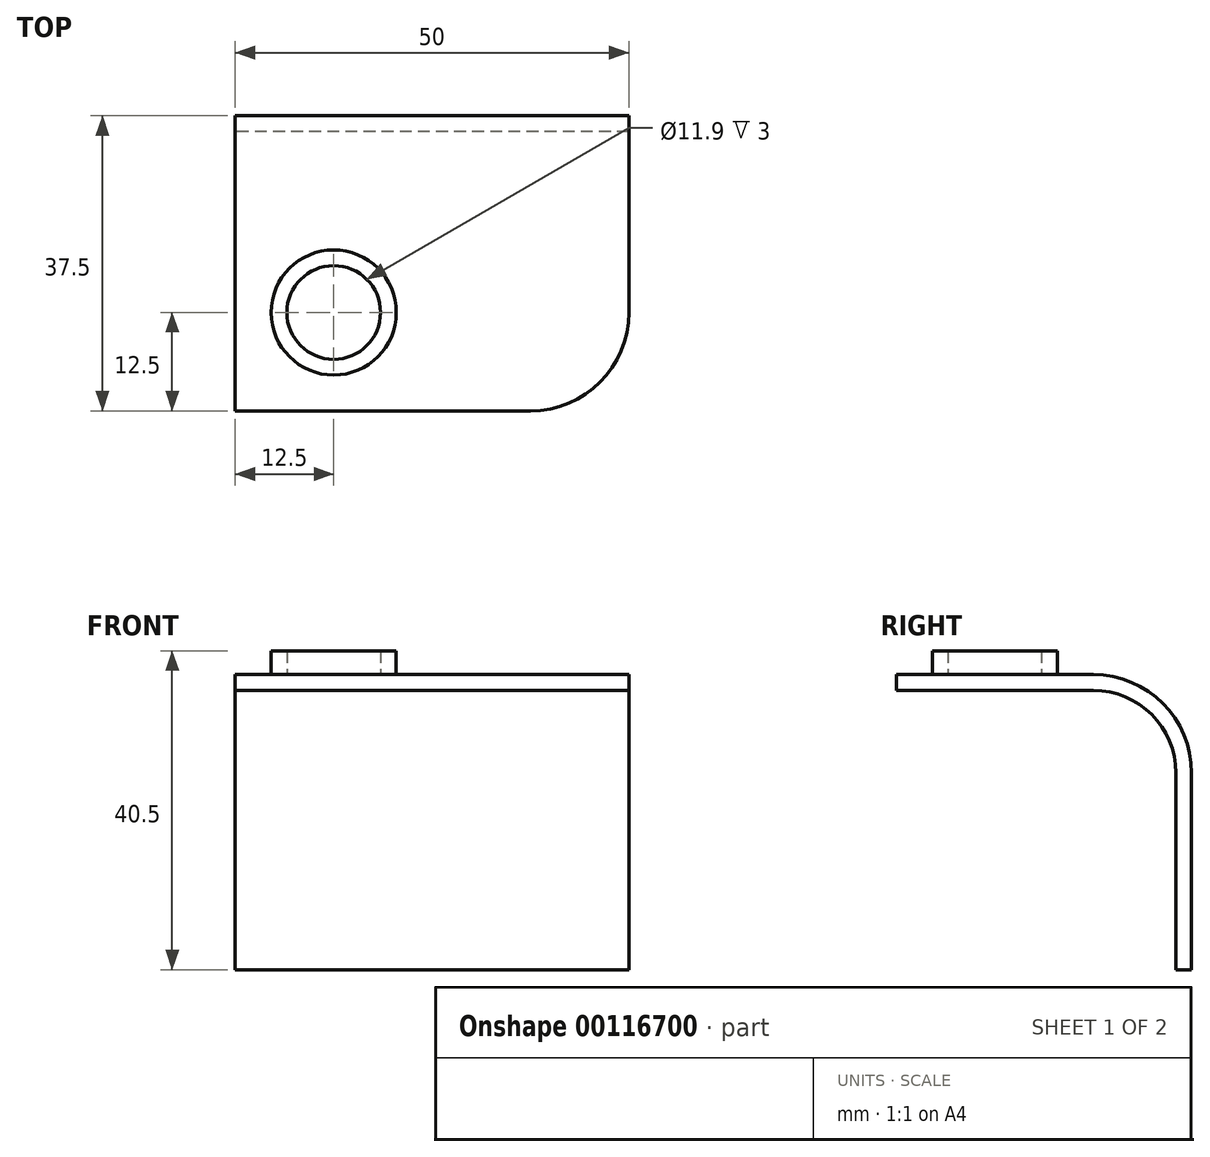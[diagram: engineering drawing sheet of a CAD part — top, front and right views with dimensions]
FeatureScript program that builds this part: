
annotation { "Feature Type Name" : "Feature", "Feature Type Description" : "" }
export const myFeature = defineFeature(function(context is Context, id is Id, definition is map)
    precondition{}
    {
        {
            var Q0;
            Q0=qCreatedBy(makeId("Front.planeOp"),FACE);
            var sketch = newSketch(context, id + "F0", { "sketchPlane" : qUnion([Q0])});
            skLineSegment(sketch, "E0.bottom", {"start": v(0, 0) * mm, "end": v(-50, 0) * mm});
            skLineSegment(sketch, "E0.top", {"start": v(0, 25) * mm, "end": v(-50, 25) * mm});
            skLineSegment(sketch, "E0.left", {"start": v(0, 0) * mm, "end": v(0, 25) * mm});
            skLineSegment(sketch, "E0.right", {"start": v(-50, 0) * mm, "end": v(-50, 25) * mm});
            skSolve(sketch);
        }
        {
            var Q0;
            Q0=makeQuery(id+"F0.imprint","IMPRINT",FACE,{"disambiguationData":[TD([[makeQuery(id+"F0.imprint","IMPRINT",EDGE,{"derivedFrom":sQuery(id+"F0.wireOp",EDGE,"E0.bottom")}),-1.0]])]});
            extrude(context, id + "F1", {"entities" : qUnion([Q0]), "depth" : 2 * mm});
        }
        {
            var Q0;
            Q0=qCreatedBy(makeId("Right.planeOp"),FACE);
            var sketch = newSketch(context, id + "F2", { "sketchPlane" : qUnion([Q0])});
            skArc(sketch, "E1", {"start": v(0, 25) * mm, "mid": v(-3.66, 33.84) * mm, "end": v(-12.5, 37.5) * mm});
            skLineSegment(sketch, "E2", {"start": v(-12.5, 37.5) * mm, "end": v(-37.5, 37.5) * mm});
            skLineSegment(sketch, "E3.0", {"start": v(-12.5, 35.5) * mm, "end": v(-37.5, 35.5) * mm});
            skArc(sketch, "E3.1", {"start": v(-2, 25) * mm, "mid": v(-5.08, 32.42) * mm, "end": v(-12.5, 35.5) * mm});
            skLineSegment(sketch, "E4", {"start": v(-2, 25) * mm, "end": v(0, 25) * mm});
            skLineSegment(sketch, "E5", {"start": v(-37.5, 35.5) * mm, "end": v(-37.5, 37.5) * mm});
            skSolve(sketch);
        }
        {
            var Q0;
            Q0 = qSketchRegion(id + "F2", true);
            var Q1;
            Q1=makeQuery(id+"F1.opExtrude","SWEPT_FACE",FACE,{"disambiguationData":[OSD([sQuery(id+"F0.wireOp",EDGE,"E0.right")])]});
            extrude(context, id + "F3", {"entities" : qUnion([Q0]), "operationType" : NewBodyOperationType.ADD, "endBound" : BoundingType.UP_TO_SURFACE, "oppositeDirection" : true, "endBoundEntityFace" : qUnion([Q1]), "depth" : 25 * mm});
        }
        {
            var Q0;
            Q0=makeQuery(id+"F3.opExtrude","TWEAK_EDGE",EDGE,{"derivedFrom":[makeQuery(id+"F1.opExtrude","SWEPT_FACE",FACE,{"disambiguationData":[OSD([sQuery(id+"F0.wireOp",EDGE,"E0.right")])]}),makeQuery(id+"F2.imprint","IMPRINT",EDGE,{"derivedFrom":sQuery(id+"F2.wireOp",EDGE,"E5")})]});
            var Q1;
            Q1=makeQuery(id+"F3.opExtrude","CAP_EDGE",EDGE,{"disambiguationData":[OSD([sQuery(id+"F2.wireOp",EDGE,"E5")])],"isStart":true});
            fillet(context, id + "F4", {"entities" : qUnion([Q0, Q1]), "radius" : 12.5 * mm, "tangentPropagation" : true, "allowEdgeOverflow" : false});
        }
        {
            var Q0;
            Q0=makeQuery(id+"F3.opExtrude","SWEPT_FACE",FACE,{"disambiguationData":[OSD([sQuery(id+"F2.wireOp",EDGE,"E2")])]});
            var sketch = newSketch(context, id + "F5", { "sketchPlane" : qUnion([Q0])});
            skCircle(sketch, "E6", {"center": v(-37.5, -25) * mm, "radius": 7.95 * mm});
            skCircle(sketch, "E7.0", {"center": v(-37.5, -25) * mm, "radius": 5.95 * mm});
            skSolve(sketch);
        }
        {
            var Q0;
            Q0 = qSketchRegion(id + "F5", true);
            extrude(context, id + "F6", {"entities" : qUnion([Q0]), "operationType" : NewBodyOperationType.ADD, "depth" : 3 * mm});
        }
    });
